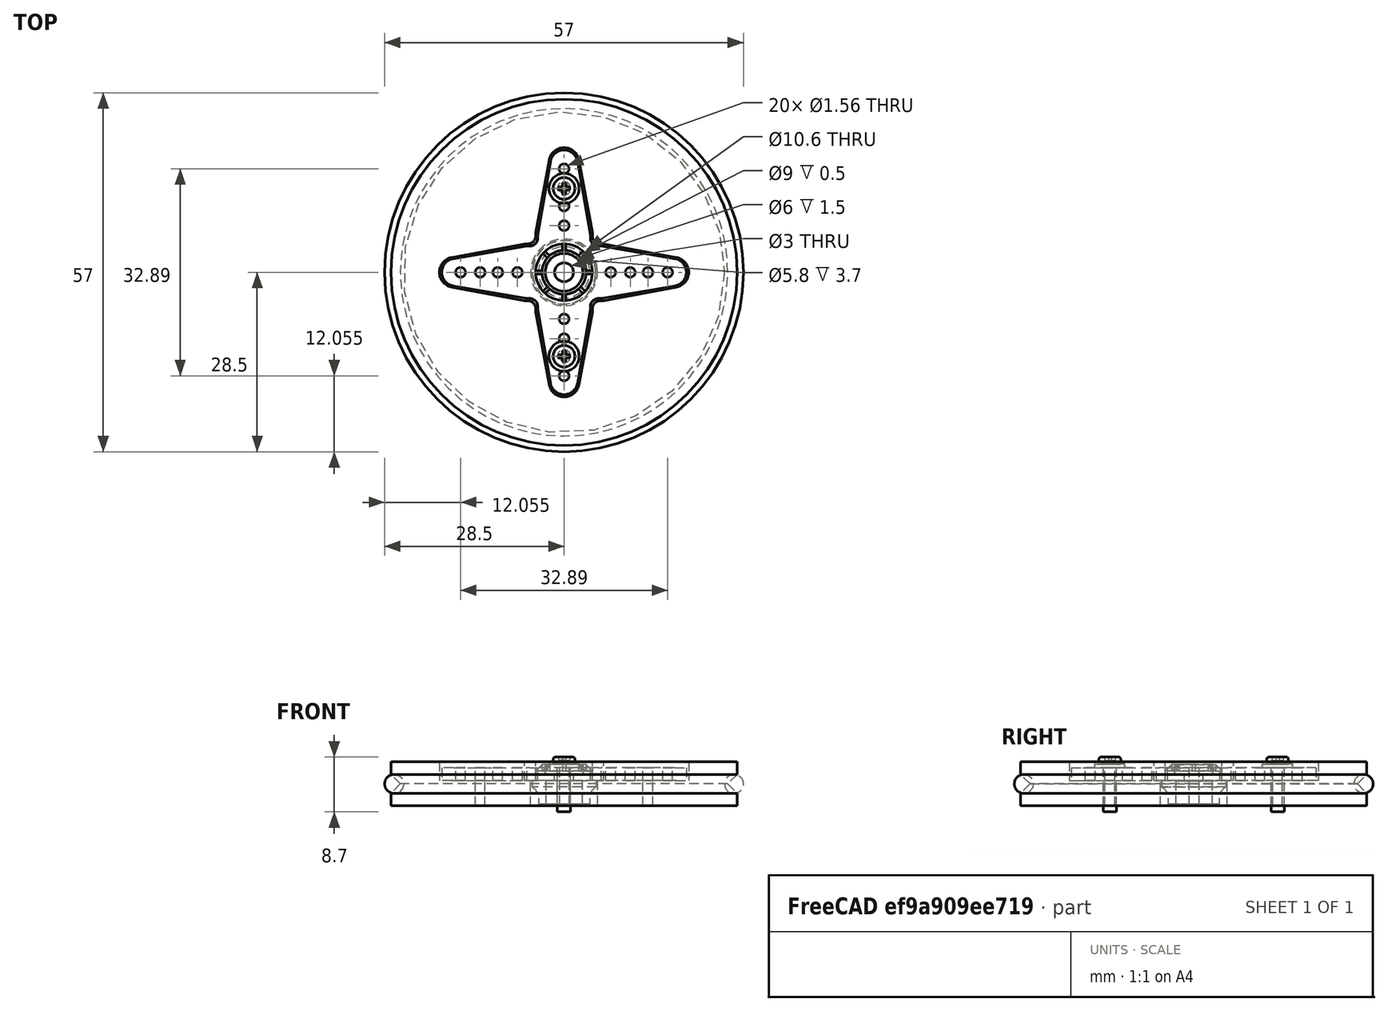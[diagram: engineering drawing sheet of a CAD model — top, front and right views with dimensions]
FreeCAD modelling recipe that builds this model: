
FCSTD DOCUMENT  (FreeCAD 0.14R3702 (Git))
Label: Miniskybot-wheel-futaba3003-4-arms-horn-assembly
License: CC-BY 3.0
LicenseURL: http://creativecommons.org/licenses/by/3.0/
objects: Part::Feature×4, Part::Torus×1, Part::Compound×1
note: 6 computed .brp shape members not serialized (recipe doc carries the construction recipe); baked Part::Feature solids carry a one-line shape summary decoded from their .brp

FEATURE [Part::Feature] PolarPattern  label="Miniskybot-wheel-futaba3003-ar-arms-horn-final"
  shape: bbox 55 x 55 x 7 mm, 36 faces (baked)
FEATURE [Part::Feature] PolarPattern001  label="4-arms-horn-final"
  Placement = pos=(0,0,0.55) rot=(0,0,1;0rad)
  shape: bbox 38.85 x 38.85 x 6.3 mm, 96 faces (baked)
FEATURE [Part::Feature] Fillet  label="bolt-002"
  Placement = pos=(0,-13.325,2.55) rot=(0,0,1;0rad)
  shape: bbox 4.8 x 4.8 x 8.7 mm, 21 faces (baked)
FEATURE [Part::Feature] Fillet001  label="bolt-1"
  Placement = pos=(0,13.325,2.55) rot=(0,0,1;0rad)
  shape: bbox 4.8 x 4.8 x 8.7 mm, 21 faces (baked)
FEATURE [Part::Torus] Torus  label="o-ring"
  Angle1 = -180
  Angle2 = 180
  Angle3 = 360
  Radius1 = 27
  Radius2 = 1.5
FEATURE [Part::Compound] Compound  label="Miniskybot-wheel-futaba3003-4-arms-horn-assembly-final"
  Links = -> [Torus,Fillet001,Fillet,PolarPattern,PolarPattern001]
